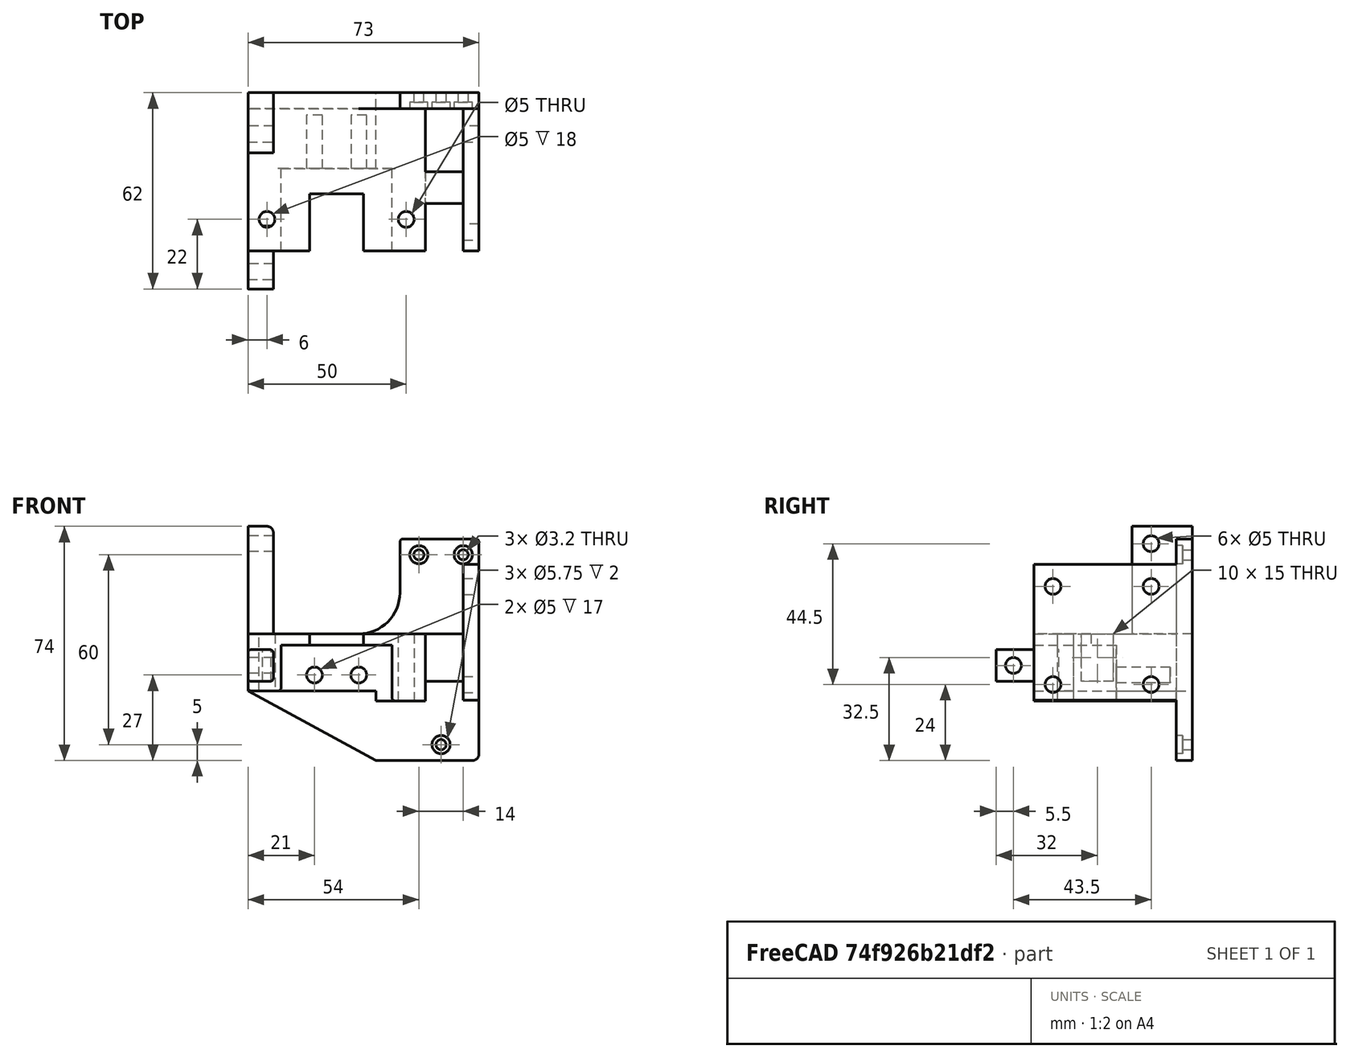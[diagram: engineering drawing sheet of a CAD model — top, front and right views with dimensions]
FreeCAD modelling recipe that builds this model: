
FCSTD DOCUMENT  (FreeCAD 0.19R)
Label: head3
License: All rights reserved
LicenseURL: http://en.wikipedia.org/wiki/All_rights_reserved
objects: Sketcher::SketchObject×17, PartDesign::Pocket×13, PartDesign::Fillet×9, PartDesign::Pad×4, PartDesign::Body×1, Mesh::Feature×1
note: 70 computed .brp shape members not serialized (recipe doc carries the construction recipe); baked Part::Feature solids carry a one-line shape summary decoded from their .brp

FEATURE [Sketcher::SketchObject] Sketch
  FullyConstrained = true
  MapMode = 5
  Support = -> [XY_Plane]
  sketch-geometry (5):
    g0: LineSegment StartX=0 StartY=0 StartZ=0 EndX=45 EndY=0 EndZ=0
    g1: LineSegment StartX=-28 StartY=0 StartZ=0 EndX=0 EndY=0 EndZ=0
    g2: LineSegment StartX=-28 StartY=0 StartZ=0 EndX=-28 EndY=-50 EndZ=0
    g3: LineSegment StartX=-28 StartY=-50 StartZ=0 EndX=45 EndY=-50 EndZ=0
    g4: LineSegment StartX=45 StartY=-50 StartZ=0 EndX=45 EndY=0 EndZ=0
  constraints (14):
    c: Coincident(g-1,g0)
    c: PointOnObject(g0,g-1)
    c: PointOnObject(g1,g-1)
    c: Coincident(g1,g0)
    c: Coincident(g1,g2)
    c: Vertical(g2)
    c: Coincident(g2,g3)
    c: Horizontal(g3)
    c: Coincident(g3,g4)
    c: Coincident(g4,g0)
    c: Vertical(g4)
    c: Distance(g4) = 50
    c: DistanceX(g0) = 45
    c: DistanceX(g1) = -28
FEATURE [PartDesign::Pad] Pad
  Direction = (1,1,1)
  Length = 70
  Length2 = 100
  Profile = -> Sketch
  Type = 0
FEATURE [Sketcher::SketchObject] Sketch001
  FullyConstrained = false
  MapMode = 5
  Placement = pos=(0,0,70) rot=(0,0,1;0rad)
  Support = -> [Pad]
  sketch-geometry (4):
    g0: LineSegment StartX=28.1122 StartY=-5 StartZ=0 EndX=40 EndY=-5 EndZ=0
    g1: LineSegment StartX=40 StartY=-5 StartZ=0 EndX=40 EndY=-51.78 EndZ=0
    g2: LineSegment StartX=40 StartY=-51.78 StartZ=0 EndX=28.1122 EndY=-51.78 EndZ=0
    g3: LineSegment StartX=28.1122 StartY=-51.78 StartZ=0 EndX=28.1122 EndY=-5 EndZ=0
  constraints (11):
    c: Coincident(g0,g1)
    c: Coincident(g1,g2)
    c: Coincident(g2,g3)
    c: Coincident(g3,g0)
    c: Horizontal(g0)
    c: Horizontal(g2)
    c: Vertical(g1)
    c: Vertical(g3)
    c: DistanceX(g0) = 40
    c: DistanceY(g1) = -51.78
    c: DistanceY(g0) = -5
FEATURE [PartDesign::Pocket] Pocket  label="BOBnotch"
  BaseFeature = -> Pad
  Length = 5
  Length2 = 100
  Profile = -> Sketch001
  Type = 1
FEATURE [Sketcher::SketchObject] Sketch002
  FullyConstrained = false
  MapMode = 5
  Placement = pos=(0,0,70) rot=(0,0,1;0rad)
  Support = -> [Pocket]
  sketch-geometry (6):
    g0: LineSegment StartX=30 StartY=-5 StartZ=0 EndX=30 EndY=-65.096 EndZ=0
    g1: LineSegment StartX=30 StartY=-65.096 StartZ=0 EndX=-40.7834 EndY=-65.096 EndZ=0
    g2: LineSegment StartX=-40.7834 StartY=-65.096 StartZ=0 EndX=-40.7834 EndY=12.9948 EndZ=0
    g3: LineSegment StartX=-40.7834 StartY=12.9948 StartZ=0 EndX=20 EndY=12.9948 EndZ=0
    g4: LineSegment StartX=20 StartY=12.9948 StartZ=0 EndX=20 EndY=-5 EndZ=0
    g5: LineSegment StartX=20 StartY=-5 StartZ=0 EndX=30 EndY=-5 EndZ=0
  constraints (15):
    c: Coincident(g0,g1)
    c: Coincident(g1,g2)
    c: Horizontal(g1)
    c: Vertical(g0)
    c: Vertical(g2)
    c: DistanceX(g0) = 30
    c: DistanceY(g0) = -5
    c: Coincident(g2,g3)
    c: Horizontal(g3)
    c: Coincident(g3,g4)
    c: Coincident(g4,g5)
    c: Coincident(g5,g0)
    c: Horizontal(g5)
    c: Vertical(g4)
    c: DistanceX(g3) = 20
FEATURE [PartDesign::Pocket] Pocket001  label="stepperplatform"
  BaseFeature = -> Pocket
  Length = 30
  Length2 = 100
  Profile = -> Sketch002
  Type = 0
FEATURE [Sketcher::SketchObject] Sketch003
  FullyConstrained = true
  MapMode = 5
  Placement = pos=(0,0,40) rot=(0,0,1;0rad)
  Support = -> [Pocket001]
  sketch-geometry (2):
    g0: Circle CenterX=-22 CenterY=-40 CenterZ=0 NormalX=0 NormalY=0 NormalZ=1 AngleXU=0 Radius=2.5
    g1: Circle CenterX=22 CenterY=-40 CenterZ=0 NormalX=0 NormalY=0 NormalZ=1 AngleXU=0 Radius=2.5
  constraints (5):
    c: Radius(g1) = 2.5
    c: Equal(g1,g0)
    c: Symmetric(g1,g0,g-2)
    c: Distance(g1,g0) = 44
    c: DistanceY(g0) = -40
FEATURE [PartDesign::Pocket] Pocket002  label="steppermountholes"
  BaseFeature = -> Pocket001
  Length = 5
  Length2 = 100
  Profile = -> Sketch003
  Type = 1
FEATURE [Sketcher::SketchObject] Sketch004
  FullyConstrained = false
  MapMode = 5
  Placement = pos=(0,0,40) rot=(0,0,1;0rad)
  Support = -> [Pocket002]
  sketch-geometry (4):
    g0: LineSegment StartX=-8.5 StartY=-32 StartZ=0 EndX=8.5 EndY=-32 EndZ=0
    g1: LineSegment StartX=8.5 StartY=-32 StartZ=0 EndX=8.5 EndY=-55.3144 EndZ=0
    g2: LineSegment StartX=8.5 StartY=-55.3144 StartZ=0 EndX=-8.5 EndY=-55.3144 EndZ=0
    g3: LineSegment StartX=-8.5 StartY=-55.3144 StartZ=0 EndX=-8.5 EndY=-32 EndZ=0
  constraints (10):
    c: Coincident(g0,g1)
    c: Coincident(g1,g2)
    c: Coincident(g2,g3)
    c: Coincident(g3,g0)
    c: Horizontal(g2)
    c: Vertical(g1)
    c: Vertical(g3)
    c: Symmetric(g0,g0,g-2)
    c: DistanceY(g0) = -32
    c: Distance(g0) = 17
FEATURE [PartDesign::Pocket] Pocket003  label="hotendnotch001"
  BaseFeature = -> Pocket002
  Length = 5
  Length2 = 100
  Profile = -> Sketch004
  Type = 1
FEATURE [Sketcher::SketchObject] Sketch005
  FullyConstrained = false
  MapMode = 5
  Placement = pos=(0,-50,0) rot=(1,0,0;1.5708rad)
  Support = -> [Pocket003]
  sketch-geometry (4):
    g0: LineSegment StartX=-17.5 StartY=36.5 StartZ=0 EndX=17.5 EndY=36.5 EndZ=0
    g1: LineSegment StartX=17.5 StartY=36.5 StartZ=0 EndX=17.5 EndY=-21.4748 EndZ=0
    g2: LineSegment StartX=17.5 StartY=-21.4748 StartZ=0 EndX=-17.5 EndY=-21.4748 EndZ=0
    g3: LineSegment StartX=-17.5 StartY=-21.4748 StartZ=0 EndX=-17.5 EndY=36.5 EndZ=0
  constraints (10):
    c: Coincident(g0,g1)
    c: Coincident(g1,g2)
    c: Coincident(g2,g3)
    c: Coincident(g3,g0)
    c: Horizontal(g2)
    c: Vertical(g1)
    c: Vertical(g3)
    c: Symmetric(g0,g0,g-2)
    c: Distance(g0) = 35
    c: DistanceY(g0) = 36.5
FEATURE [PartDesign::Pocket] Pocket004  label="hotendnotch"
  BaseFeature = -> Pocket003
  Length = 26
  Length2 = 100
  Profile = -> Sketch005
  Type = 0
FEATURE [Sketcher::SketchObject] Sketch006
  FullyConstrained = false
  MapMode = 5
  Placement = pos=(0,-24,5.9e-15) rot=(1,0,0;1.5708rad)
  Support = -> [Pocket004]
  sketch-geometry (4):
    g0: LineSegment StartX=-32.7556 StartY=22 StartZ=0 EndX=12.5 EndY=22 EndZ=0
    g1: LineSegment StartX=12.5 StartY=22 StartZ=0 EndX=12.5 EndY=-8.42821 EndZ=0
    g2: LineSegment StartX=12.5 StartY=-8.42821 StartZ=0 EndX=-32.7556 EndY=-8.42821 EndZ=0
    g3: LineSegment StartX=-32.7556 StartY=-8.42821 StartZ=0 EndX=-32.7556 EndY=22 EndZ=0
  constraints (10):
    c: Coincident(g0,g1)
    c: Coincident(g1,g2)
    c: Coincident(g2,g3)
    c: Coincident(g3,g0)
    c: Horizontal(g0)
    c: Horizontal(g2)
    c: Vertical(g1)
    c: Vertical(g3)
    c: DistanceY(g0) = 22
    c: DistanceX(g0) = 12.5
FEATURE [PartDesign::Pocket] Pocket005  label="fanclearance"
  BaseFeature = -> Pocket004
  Length = 28
  Length2 = 100
  Profile = -> Sketch006
  Type = 4
FEATURE [Sketcher::SketchObject] Sketch007
  FullyConstrained = false
  MapMode = 5
  Placement = pos=(0,-50,0) rot=(1,0,0;1.5708rad)
  Support = -> [Pocket005]
  sketch-geometry (4):
    g0: LineSegment StartX=7.61208 StartY=18.8386 StartZ=0 EndX=33.8542 EndY=18.8386 EndZ=0
    g1: LineSegment StartX=33.8542 StartY=18.8386 StartZ=0 EndX=33.8542 EndY=-10.9025 EndZ=0
    g2: LineSegment StartX=33.8542 StartY=-10.9025 StartZ=0 EndX=7.61208 EndY=-10.9025 EndZ=0
    g3: LineSegment StartX=7.61208 StartY=-10.9025 StartZ=0 EndX=7.61208 EndY=18.8386 EndZ=0
  constraints (8):
    c: Coincident(g0,g1)
    c: Coincident(g1,g2)
    c: Coincident(g2,g3)
    c: Coincident(g3,g0)
    c: Horizontal(g0)
    c: Horizontal(g2)
    c: Vertical(g1)
    c: Vertical(g3)
FEATURE [PartDesign::Pocket] Pocket006  label="bottomconnectorclearance"
  BaseFeature = -> Pocket005
  Length = 45
  Length2 = 100
  Profile = -> Sketch007
  Type = 0
FEATURE [Sketcher::SketchObject] Sketch008
  FullyConstrained = false
  MapMode = 5
  Placement = pos=(0,-50,0) rot=(1,0,0;1.5708rad)
  Support = -> [Pocket006]
  sketch-geometry (8):
    g0: LineSegment StartX=35.0962 StartY=76.3926 StartZ=0 EndX=50.7218 EndY=76.3926 EndZ=0
    g1: LineSegment StartX=50.7218 StartY=76.3926 StartZ=0 EndX=50.7218 EndY=62 EndZ=0
    g2: LineSegment StartX=50.7218 StartY=62 StartZ=0 EndX=35.0962 EndY=62 EndZ=0
    g3: LineSegment StartX=35.0962 StartY=62 StartZ=0 EndX=35.0962 EndY=76.3926 EndZ=0
    g4: LineSegment StartX=34.0545 StartY=19 StartZ=0 EndX=58.6648 EndY=19 EndZ=0
    g5: LineSegment StartX=58.6648 StartY=19 StartZ=0 EndX=58.6648 EndY=-12.6735 EndZ=0
    g6: LineSegment StartX=58.6648 StartY=-12.6735 StartZ=0 EndX=34.0545 EndY=-12.6735 EndZ=0
    g7: LineSegment StartX=34.0545 StartY=-12.6735 StartZ=0 EndX=34.0545 EndY=19 EndZ=0
  constraints (18):
    c: Coincident(g0,g1)
    c: Coincident(g1,g2)
    c: Coincident(g2,g3)
    c: Coincident(g3,g0)
    c: Horizontal(g0)
    c: Horizontal(g2)
    c: Vertical(g1)
    c: Vertical(g3)
    c: Coincident(g4,g5)
    c: Coincident(g5,g6)
    c: Coincident(g6,g7)
    c: Coincident(g7,g4)
    c: Horizontal(g4)
    c: Horizontal(g6)
    c: Vertical(g5)
    c: Vertical(g7)
    c: DistanceY(g2) = 62
    c: DistanceY(g4) = 19
FEATURE [PartDesign::Pocket] Pocket007  label="BOBnotches"
  BaseFeature = -> Pocket006
  Length = 45
  Length2 = 100
  Profile = -> Sketch008
  Type = 0
FEATURE [Sketcher::SketchObject] Sketch009
  FullyConstrained = true
  MapMode = 5
  Placement = pos=(45,0,0) rot=(0.57735,0.57735,0.57735;2.0944rad)
  Support = -> [Pocket007]
  sketch-geometry (5):
    g0: Circle CenterX=-44 CenterY=55 CenterZ=0 NormalX=0 NormalY=0 NormalZ=1 AngleXU=0 Radius=2.5
    g1: Circle CenterX=-13 CenterY=24 CenterZ=0 NormalX=0 NormalY=0 NormalZ=1 AngleXU=0 Radius=2.5
    g2: LineSegment StartX=-44 StartY=55 StartZ=0 EndX=-13 EndY=24 EndZ=0
    g3: Circle CenterX=-13 CenterY=55 CenterZ=0 NormalX=0 NormalY=0 NormalZ=1 AngleXU=0 Radius=2.5
    g4: Circle CenterX=-44 CenterY=24 CenterZ=0 NormalX=0 NormalY=0 NormalZ=1 AngleXU=0 Radius=2.5
  constraints (14):
    c: Coincident(g2,g0)
    c: Coincident(g2,g1)
    c: Angle(g2) = -0.785398
    c: DistanceX(g1) = -13
    c: DistanceY(g1) = 24
    c: Diameter(g4) = 5
    c: Equal(g4,g0)
    c: Equal(g4,g3)
    c: Equal(g4,g1)
    c: DistanceY(g4,g0) = 31
    c: DistanceX(g0,g3) = 31
    c: DistanceX(g4,g1) = 31
    c: DistanceY(g4) = 24
    c: DistanceY(g1,g3) = 31
FEATURE [PartDesign::Pocket] Pocket008  label="stepperholes"
  BaseFeature = -> Pocket007
  Length = 13
  Length2 = 100
  Profile = -> Sketch009
  Type = 0
FEATURE [Sketcher::SketchObject] Sketch010
  FullyConstrained = true
  MapMode = 5
  Placement = pos=(0,0,0) rot=(0,0.707107,0.707107;3.14159rad)
  Support = -> [Pocket008]
  sketch-geometry (3):
    g0: Circle CenterX=-33 CenterY=5 CenterZ=0 NormalX=0 NormalY=0 NormalZ=1 AngleXU=0 Radius=1.6
    g1: Circle CenterX=-40 CenterY=65 CenterZ=0 NormalX=0 NormalY=0 NormalZ=1 AngleXU=0 Radius=1.6
    g2: Circle CenterX=-26 CenterY=65 CenterZ=0 NormalX=0 NormalY=0 NormalZ=1 AngleXU=0 Radius=1.6
  constraints (9):
    c: Diameter(g0) = 3.2
    c: Equal(g0,g2)
    c: Equal(g0,g1)
    c: DistanceX(g0) = -33
    c: Distance(g1,g2) = 14
    c: DistanceX(g2) = -26
    c: DistanceY(g0) = 5
    c: DistanceY(g2) = 65
    c: DistanceY(g1) = 65
FEATURE [PartDesign::Pocket] Pocket009  label="mountholes"
  BaseFeature = -> Pocket008
  Length = 5
  Length2 = 100
  Profile = -> Sketch010
  Type = 0
FEATURE [Sketcher::SketchObject] Sketch014
  FullyConstrained = true
  MapMode = 5
  Placement = pos=(45,0,0) rot=(0.57735,0.57735,0.57735;2.0944rad)
  Support = -> [Pocket009]
  sketch-geometry (4):
    g0: LineSegment StartX=-35 StartY=40 StartZ=0 EndX=-25 EndY=40 EndZ=0
    g1: LineSegment StartX=-25 StartY=40 StartZ=0 EndX=-25 EndY=25 EndZ=0
    g2: LineSegment StartX=-25 StartY=25 StartZ=0 EndX=-35 EndY=25 EndZ=0
    g3: LineSegment StartX=-35 StartY=25 StartZ=0 EndX=-35 EndY=40 EndZ=0
  constraints (12):
    c: Coincident(g0,g1)
    c: Coincident(g1,g2)
    c: Coincident(g2,g3)
    c: Coincident(g3,g0)
    c: Horizontal(g0)
    c: Horizontal(g2)
    c: Vertical(g1)
    c: Vertical(g3)
    c: Distance(g1) = 15
    c: Distance(g0) = 10
    c: DistanceX(g0) = -25
    c: DistanceY(g1) = 25
FEATURE [PartDesign::Pad] Pad001
  BaseFeature = -> Pocket009
  Direction = (1,1,1)
  Length = 23
  Length2 = 100
  Profile = -> Sketch014
  Reversed = true
  Type = 0
FEATURE [Sketcher::SketchObject] Sketch015
  FullyConstrained = false
  MapMode = 5
  Placement = pos=(-28,0,0) rot=(0.57735,-0.57735,-0.57735;2.0944rad)
  Support = -> [Pad001]
  sketch-geometry (8):
    g0: LineSegment StartX=0 StartY=74 StartZ=0 EndX=19 EndY=74 EndZ=0
    g1: LineSegment StartX=19 StartY=74 StartZ=0 EndX=19 EndY=35.8156 EndZ=0
    g2: LineSegment StartX=19 StartY=35.8156 StartZ=0 EndX=0 EndY=35.8156 EndZ=0
    g3: LineSegment StartX=0 StartY=35.8156 StartZ=0 EndX=0 EndY=74 EndZ=0
    g4: LineSegment StartX=42.1188 StartY=35 StartZ=0 EndX=62 EndY=35 EndZ=0
    g5: LineSegment StartX=62 StartY=35 StartZ=0 EndX=62 EndY=25 EndZ=0
    g6: LineSegment StartX=62 StartY=25 StartZ=0 EndX=42.1188 EndY=25 EndZ=0
    g7: LineSegment StartX=42.1188 StartY=25 StartZ=0 EndX=42.1188 EndY=35 EndZ=0
  constraints (21):
    c: Coincident(g0,g1)
    c: Coincident(g1,g2)
    c: Coincident(g2,g3)
    c: Coincident(g3,g0)
    c: Horizontal(g0)
    c: Horizontal(g2)
    c: Vertical(g1)
    c: Vertical(g3)
    c: Distance(g0) = 19
    c: DistanceY(g0) = 74
    c: Coincident(g4,g5)
    c: Coincident(g5,g6)
    c: Coincident(g6,g7)
    c: Coincident(g7,g4)
    c: Horizontal(g4)
    c: Horizontal(g6)
    c: Vertical(g5)
    c: Vertical(g7)
    c: DistanceX(g4) = 62
    c: DistanceY(g4) = 35
    c: DistanceY(g5) = 25
FEATURE [PartDesign::Pad] Pad002  label="fanbosses"
  BaseFeature = -> Pad001
  Direction = (1,1,1)
  Length = 8
  Length2 = 100
  Profile = -> Sketch015
  Reversed = true
  Type = 0
FEATURE [Sketcher::SketchObject] Sketch011
  FullyConstrained = true
  MapMode = 5
  Placement = pos=(-28,0,0) rot=(0.57735,-0.57735,-0.57735;2.0944rad)
  Support = -> [Pad002]
  sketch-geometry (3):
    g0: Circle CenterX=56.5 CenterY=30 CenterZ=0 NormalX=0 NormalY=0 NormalZ=1 AngleXU=0 Radius=2.5
    g1: Circle CenterX=13 CenterY=68.5 CenterZ=0 NormalX=0 NormalY=0 NormalZ=1 AngleXU=0 Radius=2.5
    g2: GeomPoint X=36 Y=48 Z=0
  constraints (8):
    c: Diameter(g0) = 5
    c: DistanceY(g0) = 30
    c: Diameter(g1) = 5
    c: DistanceX(g1) = 13
    c: DistanceY(g0,g2) = 18
    c: DistanceY(g2,g1) = 20.5
    c: DistanceX(g2,g0) = 20.5
    c: DistanceX(g1,g2) = 23
FEATURE [Sketcher::SketchObject] Sketch013
  ExternalGeometry = -> [Pad002]
  FullyConstrained = true
  MapMode = 5
  Placement = pos=(0,-24,5.9e-15) rot=(1,0,0;1.5708rad)
  Support = -> [Pad002]
  sketch-geometry (2):
    g0: Circle CenterX=-7 CenterY=27 CenterZ=0 NormalX=0 NormalY=0 NormalZ=1 AngleXU=0 Radius=2.5
    g1: Circle CenterX=7 CenterY=27 CenterZ=0 NormalX=0 NormalY=0 NormalZ=1 AngleXU=0 Radius=2.5
  constraints (5):
    c: Symmetric(g1,g0,g-2)
    c: Distance(g1,g0) = 14
    c: Diameter(g1) = 5
    c: Equal(g1,g0)
    c: DistanceY(g1,g-3) = 9.5
FEATURE [PartDesign::Pocket] Pocket010
  BaseFeature = -> Pad002
  Length = 17
  Length2 = 100
  Profile = -> Sketch013
  Type = 0
FEATURE [PartDesign::Pocket] Pocket011
  BaseFeature = -> Pocket010
  Length = 15
  Length2 = 100
  Profile = -> Sketch011
  Type = 0
FEATURE [Sketcher::SketchObject] Sketch016
  ExternalGeometry = -> [Pocket011]
  FullyConstrained = false
  MapMode = 5
  Placement = pos=(0,0,0) rot=(0,0.707107,0.707107;3.14159rad)
  Support = -> [Pocket011]
  sketch-geometry (3):
    g0: LineSegment StartX=-12.5 StartY=0 StartZ=0 EndX=28 EndY=22 EndZ=0
    g1: LineSegment StartX=28 StartY=22 StartZ=0 EndX=-20.7119 EndY=22 EndZ=0
    g2: LineSegment StartX=-20.7119 StartY=22 StartZ=0 EndX=-12.5 EndY=0 EndZ=0
  constraints (6):
    c: Coincident(g0,g1)
    c: Horizontal(g1)
    c: Coincident(g1,g2)
    c: Coincident(g2,g0)
    c: Coincident(g0,g-3)
    c: Coincident(g0,g-4)
FEATURE [PartDesign::Pad] Pad003
  BaseFeature = -> Pocket011
  Direction = (1,1,1)
  Length = 5
  Length2 = 100
  Profile = -> Sketch016
  Reversed = true
  Type = 0
FEATURE [PartDesign::Fillet] Fillet
  Base = -> Pad003 [Edge44]
  BaseFeature = -> Pad003
  Radius = 13
  SupportTransform = false
FEATURE [PartDesign::Fillet] Fillet001
  Base = -> Fillet [Edge46]
  BaseFeature = -> Fillet
  Radius = 2
  SupportTransform = false
FEATURE [PartDesign::Fillet] Fillet002
  Base = -> Fillet001 [Edge19]
  BaseFeature = -> Fillet001
  Radius = 1
  SupportTransform = false
FEATURE [PartDesign::Fillet] Fillet003
  Base = -> Fillet002 [Edge38]
  BaseFeature = -> Fillet002
  Radius = 1
  SupportTransform = false
FEATURE [PartDesign::Fillet] Fillet004
  Base = -> Fillet003 [Edge137]
  BaseFeature = -> Fillet003
  Radius = 1
  SupportTransform = false
FEATURE [PartDesign::Fillet] Fillet005
  Base = -> Fillet004 [Edge143]
  BaseFeature = -> Fillet004
  Radius = 1
  SupportTransform = false
FEATURE [PartDesign::Fillet] Fillet006
  Base = -> Fillet005 [Edge137]
  BaseFeature = -> Fillet005
  Radius = 1
  SupportTransform = false
FEATURE [PartDesign::Fillet] Fillet007
  Base = -> Fillet006 [Edge170]
  BaseFeature = -> Fillet006
  Radius = 2
  SupportTransform = false
FEATURE [PartDesign::Fillet] Fillet008
  Base = -> Fillet007 [Edge193,Edge195,Edge192,Edge198]
  BaseFeature = -> Fillet007
  Radius = 1
  SupportTransform = false
FEATURE [Sketcher::SketchObject] Sketch017
  ExternalGeometry = -> [Fillet008]
  FullyConstrained = true
  MapMode = 5
  Placement = pos=(0,-5,0) rot=(1,0,0;1.5708rad)
  Support = -> [Fillet008]
  sketch-geometry (3):
    g0: Circle CenterX=26 CenterY=65 CenterZ=0 NormalX=0 NormalY=0 NormalZ=1 AngleXU=0 Radius=2.875
    g1: Circle CenterX=40 CenterY=65 CenterZ=0 NormalX=0 NormalY=0 NormalZ=1 AngleXU=0 Radius=2.875
    g2: Circle CenterX=33 CenterY=5 CenterZ=0 NormalX=0 NormalY=0 NormalZ=1 AngleXU=0 Radius=2.875
  constraints (6):
    c: Diameter(g2) = 5.75
    c: Equal(g2,g1)
    c: Equal(g2,g0)
    c: Coincident(g0,g-4)
    c: Coincident(g1,g-3)
    c: Coincident(g2,g-5)
FEATURE [PartDesign::Pocket] Pocket012
  BaseFeature = -> Fillet008
  Length = 2
  Length2 = 100
  Profile = -> Sketch017
  Type = 0
FEATURE [PartDesign::Body] Body
  Group = -> [Sketch,Pad,Sketch001,Pocket,Sketch002,Pocket001,Sketch003,Pocket002,Sketch004,Pocket003,Sketch005,Pocket004,Sketch006,Pocket005,Sketch007,Pocket006,Sketch008,Pocket007,Sketch009,Pocket008,Sketch010,Pocket009,Sketch011,Sketch013,Sketch014,Pad001,Sketch015,Pad002,Pocket010,Pocket011,Sketch016,Pad003,Fillet,Fillet001,Fillet002,Fillet003,Fillet004,Fillet005,Fillet006,Fillet007,Fillet008,Sketch017,+1 more]
  Origin = -> Origin
  Tip = -> Pocket012
FEATURE [Mesh::Feature] Mesh  label="Pocket012 (Meshed)"
